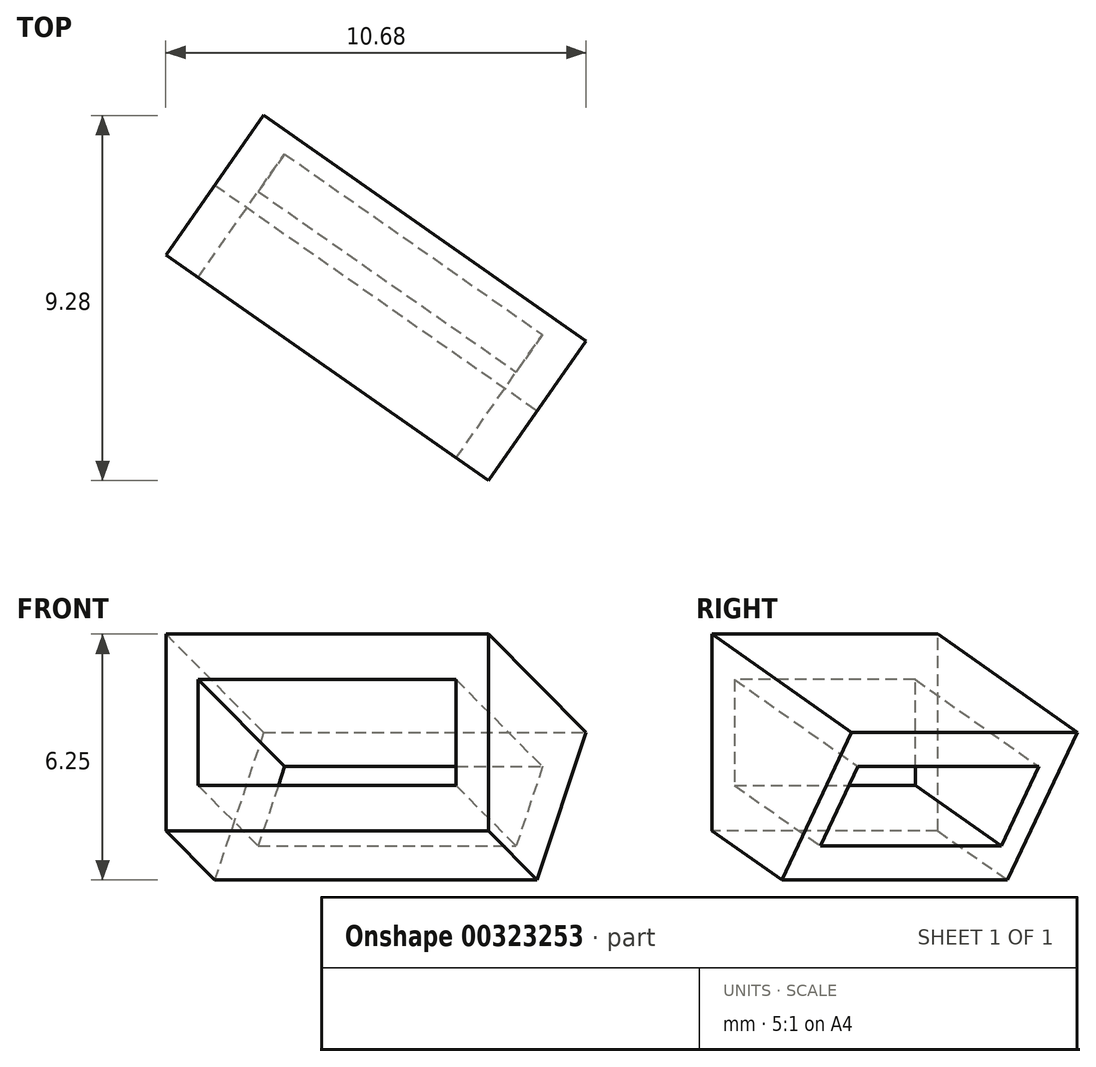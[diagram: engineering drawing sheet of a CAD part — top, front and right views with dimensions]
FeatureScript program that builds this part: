
annotation { "Feature Type Name" : "Feature", "Feature Type Description" : "" }
export const myFeature = defineFeature(function(context is Context, id is Id, definition is map)
    precondition{}
    {
        {
            var Q0;
            Q0=qCreatedBy(makeId("Top.planeOp"),FACE);
            var sketch = newSketch(context, id + "F0", { "sketchPlane" : qUnion([Q0])});
            skCircle(sketch, "E0", {"center": v(0, 0) * mm, "radius": 0.5 * mm});
            skSolve(sketch);
        }
        {
            var Q0;
            Q0=qCreatedBy(makeId("Top.planeOp"),FACE);
            var sketch = newSketch(context, id + "F1", { "sketchPlane" : qUnion([Q0])});
            skCircle(sketch, "E1", {"center": v(0, 0) * mm, "radius": 32.7 * mm, "construction": true});
            skPoint(sketch, "E2", {"position": v(8.47, 31.6) * mm});
            skPoint(sketch, "E3", {"position": v(-18.76, -26.8) * mm});
            skLineSegment(sketch, "E4", {"start": v(-18.76, -26.8) * mm, "end": v(0, 0) * mm, "construction": true});
            skLineSegment(sketch, "E5", {"start": v(0, 0) * mm, "end": v(8.47, 31.6) * mm, "construction": true});
            skLineSegment(sketch, "E6", {"start": v(0, 0) * mm, "end": v(0, -32.7) * mm, "construction": true});
            skSolve(sketch);
        }
        {
            var Q0;
            Q0=sQuery(id+"F1.wireOp",VERTEX,"E4.start");
            var Q1;
            Q1=sQuery(id+"F1.wireOp",EDGE,"E4");
            cPlane(context, id + "F2", {"entities" : qUnion([Q0, Q1]), "cplaneType" : CPlaneType.LINE_POINT, "offset" : 25 * mm, "width" : 150 * mm, "height" : 150 * mm});
        }
        {
            var Q0;
            Q0=qCreatedBy(id+"F2.planeOp",FACE);
            var sketch = newSketch(context, id + "F3", { "sketchPlane" : qUnion([Q0])});
            skLineSegment(sketch, "E7.bottom", {"start": v(5, -7.5) * mm, "end": v(-5, -7.5) * mm});
            skLineSegment(sketch, "E7.top", {"start": v(5, -2.5) * mm, "end": v(-5, -2.5) * mm});
            skLineSegment(sketch, "E7.left", {"start": v(5, -7.5) * mm, "end": v(5, -2.5) * mm});
            skLineSegment(sketch, "E7.right", {"start": v(-5, -7.5) * mm, "end": v(-5, -2.5) * mm});
            skPoint(sketch, "E7.middle", {"position": v(0, -5) * mm});
            skLineSegment(sketch, "E8", {"start": v(0, -5) * mm, "end": v(0, 0) * mm, "construction": true});
            skSolve(sketch);
        }
        {
            var Q0;
            Q0=qCreatedBy(id+"F2.planeOp",FACE);
            var Q1;
            Q1=sQuery(id+"F3.wireOp",EDGE,"E8");
            cPlane(context, id + "F4", {"entities" : qUnion([Q0, Q1]), "cplaneType" : CPlaneType.LINE_ANGLE, "offset" : 25 * mm, "angle" : 90 * degree, "width" : 150 * mm, "height" : 150 * mm});
        }
        {
            var Q0;
            Q0=qCreatedBy(id+"F4.planeOp",FACE);
            var sketch = newSketch(context, id + "F5", { "sketchPlane" : qUnion([Q0])});
            skLineSegment(sketch, "E9", {"start": v(-32.7, -5) * mm, "end": v(-28.38, -7.5) * mm});
            skLineSegment(sketch, "E10", {"start": v(-28.38, -7.5) * mm, "end": v(-32.7, -5) * mm});
            skSolve(sketch);
        }
        {
            var Q0;
            Q0=makeQuery(id+"F3.imprint","IMPRINT",FACE,{"disambiguationData":[TD([[makeQuery(id+"F3.imprint","IMPRINT",EDGE,{"derivedFrom":sQuery(id+"F3.wireOp",EDGE,"E7.bottom")}),-1.0]])]});
            var Q1;
            Q1=sQuery(id+"F5.wireOp",EDGE,"E10");
            sweep(context, id + "F6", {"profiles" : qUnion([Q0]), "path" : qUnion([Q1])});
        }
        {
            var Q0;
            Q0=makeQuery(id+"F6.opSweep","SWEPT_FACE",FACE,{"disambiguationData":[OSD([sQuery(id+"F3.wireOp",EDGE,"E7.right"),sQuery(id+"F5.wireOp",EDGE,"E10")])]});
            var sketch = newSketch(context, id + "F7", { "sketchPlane" : qUnion([Q0])});
            skLineSegment(sketch, "E11", {"start": v(-28.38, -5) * mm, "end": v(-30.54, -8.75) * mm});
            skLineSegment(sketch, "E12", {"start": v(-30.54, -8.75) * mm, "end": v(-28.38, -10) * mm});
            skLineSegment(sketch, "E13", {"start": v(-28.38, -10) * mm, "end": v(-28.38, -5) * mm});
            skSolve(sketch);
        }
        {
            var Q0;
            Q0=makeQuery(id+"F7.imprint","IMPRINT",FACE,{"disambiguationData":[TD([[makeQuery(id+"F7.imprint","IMPRINT",EDGE,{"derivedFrom":sQuery(id+"F7.wireOp",EDGE,"E11")}),1.0]])]});
            extrude(context, id + "F8", {"entities" : qUnion([Q0]), "operationType" : NewBodyOperationType.REMOVE, "endBound" : BoundingType.UP_TO_NEXT, "oppositeDirection" : true, "depth" : 25 * mm});
        }
        {
            var Q0;
            Q0=makeQuery(id+"F8.boolean.opBoolean","COPY",FACE,{"derivedFrom":makeQuery(id+"F8.opExtrude","SWEPT_FACE",FACE,{"disambiguationData":[OSD([sQuery(id+"F7.wireOp",EDGE,"E11")])]})});
            var Q1;
            Q1=makeQuery(id+"F6.opSweep","CAP_FACE",FACE,{"disambiguationData":[OSD([sQuery(id+"F3.wireOp",EDGE,"E7.bottom"),sQuery(id+"F3.wireOp",EDGE,"E7.top"),sQuery(id+"F3.wireOp",EDGE,"E7.left"),sQuery(id+"F3.wireOp",EDGE,"E7.right"),sQuery(id+"F5.wireOp",VERTEX,"E10.end")])],"isStart":true});
            shell(context, id + "F9", {"entities" : qUnion([Q0, Q1]), "thickness" : 1 * mm});
        }
    });
